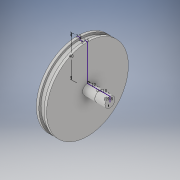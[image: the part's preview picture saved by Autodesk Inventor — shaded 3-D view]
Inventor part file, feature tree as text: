
AUTODESK INVENTOR PART (.ipt)
format: ipt  version: 2019 (Build 230136000, 136)  size: 265,728 bytes
history: native  units: in
note: dims shown in document units (in); Inventor stores cm internally (conversion verified against a paired STEP export)
features: revolve x1, sketch x1
ambient origin geometry x8: Origin, YZ Plane, XZ Plane, XY Plane, X Axis, Y Axis, Z Axis, Center Point
bodies: Solid1 (feature_tree)
feature tree (2):
  revolve  "Revolution1"  [1 undecoded]
  sketch  "Sketch1"  dims[d0=1.5748in d1=0.0984in d2=0.0787in d3=0.1969in d4=0.0984in d6=0.4724in d7=0.0039in d8=0.3937in d9=90.0deg d11=0.3858in]
note: 1 required parameter value undecoded (feature->parameter linkage not recoverable at this tier; creation-order binding heuristic only, values carry confidence <= 0.55)
